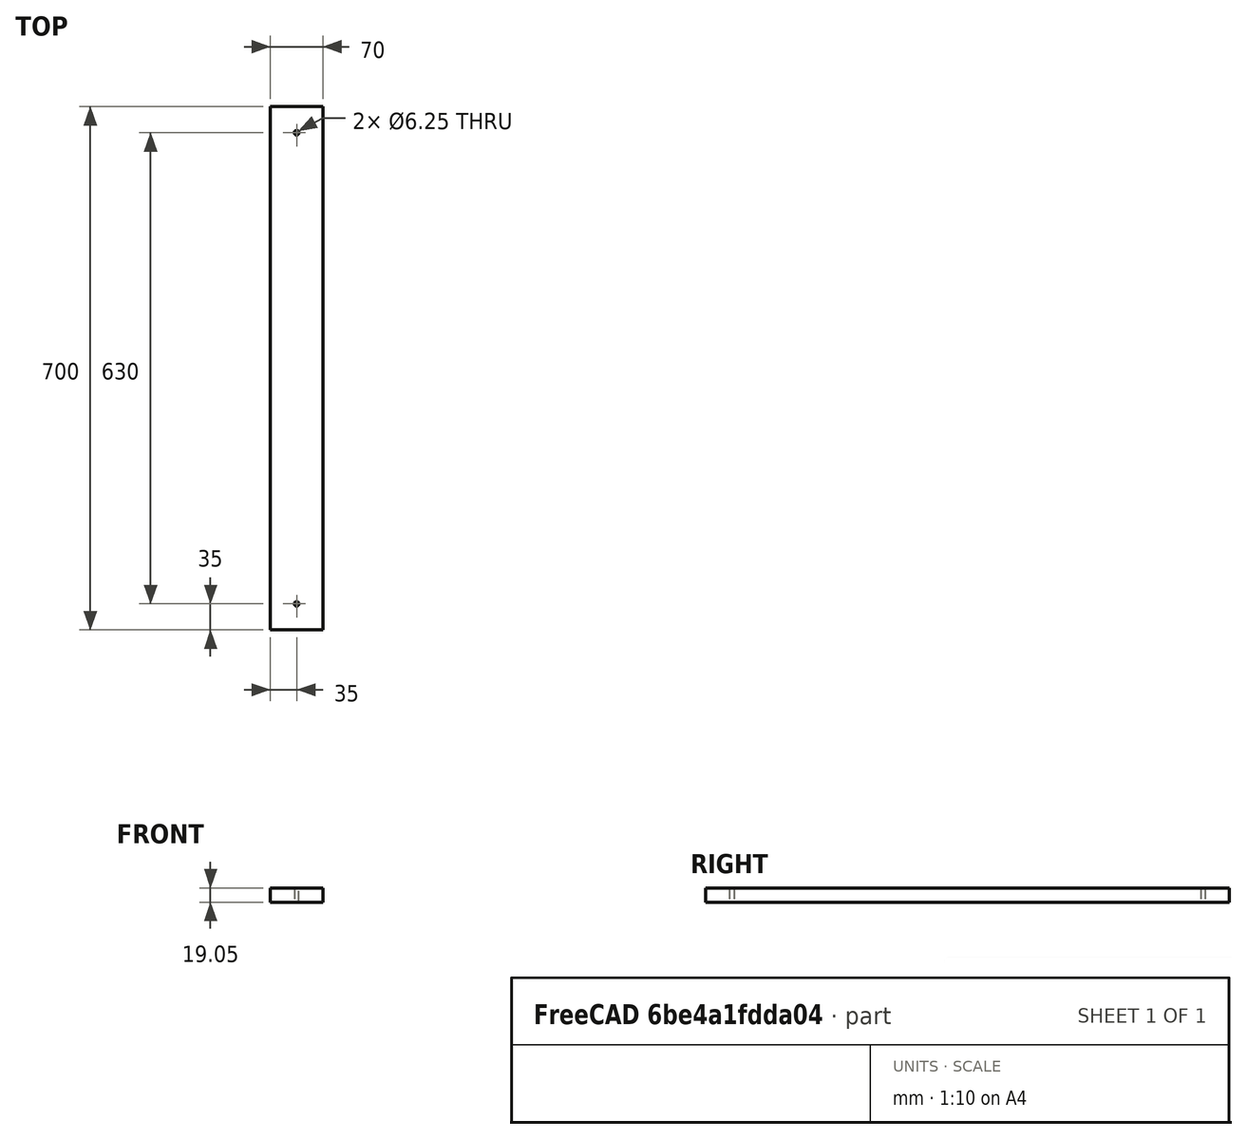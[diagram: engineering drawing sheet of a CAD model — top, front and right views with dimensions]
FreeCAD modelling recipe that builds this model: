
FCSTD DOCUMENT  (FreeCAD 0.20R29410 (Git))
Label: foot
License: All rights reserved
LicenseURL: http://en.wikipedia.org/wiki/All_rights_reserved
objects: Sketcher::SketchObject×1, PartDesign::Pad×1, PartDesign::Body×1
note: 4 computed .brp shape members not serialized (recipe doc carries the construction recipe); baked Part::Feature solids carry a one-line shape summary decoded from their .brp

FEATURE [Sketcher::SketchObject] Sketch
  FullyConstrained = true
  MapMode = 5
  Support = -> [XY_Plane]
  sketch-geometry (14):
    g0: LineSegment StartX=-35 StartY=350 StartZ=0 EndX=35 EndY=350 EndZ=0
    g1: LineSegment StartX=35 StartY=350 StartZ=0 EndX=35 EndY=-350 EndZ=0
    g2: LineSegment StartX=35 StartY=-350 StartZ=0 EndX=-35 EndY=-350 EndZ=0
    g3: LineSegment StartX=-35 StartY=-350 StartZ=0 EndX=-35 EndY=350 EndZ=0
    g4: Circle CenterX=6e-16 CenterY=315 CenterZ=0 NormalX=0 NormalY=0 NormalZ=1 AngleXU=0 Radius=3.125
    g5: Circle CenterX=0 CenterY=-315 CenterZ=0 NormalX=0 NormalY=0 NormalZ=1 AngleXU=0 Radius=3.125
    g6: LineSegment StartX=-35 StartY=-280 StartZ=0 EndX=35 EndY=-280 EndZ=0
    g7: LineSegment StartX=35 StartY=-280 StartZ=0 EndX=35 EndY=-350 EndZ=0
    g8: LineSegment StartX=35 StartY=-350 StartZ=0 EndX=-35 EndY=-350 EndZ=0
    g9: LineSegment StartX=-35 StartY=-350 StartZ=0 EndX=-35 EndY=-280 EndZ=0
    g10: LineSegment StartX=-35 StartY=350 StartZ=0 EndX=35 EndY=350 EndZ=0
    g11: LineSegment StartX=35 StartY=350 StartZ=0 EndX=35 EndY=280 EndZ=0
    g12: LineSegment StartX=35 StartY=280 StartZ=0 EndX=-35 EndY=280 EndZ=0
    g13: LineSegment StartX=-35 StartY=280 StartZ=0 EndX=-35 EndY=350 EndZ=0
  constraints (40):
    c: Coincident(g0,g1)
    c: Coincident(g1,g2)
    c: Coincident(g2,g3)
    c: Coincident(g3,g0)
    c: Horizontal(g0)
    c: Horizontal(g2)
    c: Vertical(g1)
    c: Vertical(g3)
    c: DistanceY(g-1,g4) = 315
    c: DistanceY(g5,g-1) = 315
    c: Coincident(g6,g7)
    c: Coincident(g7,g8)
    c: Coincident(g8,g9)
    c: Coincident(g9,g6)
    c: Horizontal(g6)
    c: Horizontal(g8)
    c: Vertical(g7)
    c: Vertical(g9)
    c: Symmetric(g6,g7,g5)
    c: PointOnObject(g5,g-2)
    c: PointOnObject(g4,g-2)
    c: DistanceX(g8,g8) = 70
    c: Equal(g8,g9)
    c: Coincident(g10,g11)
    c: Coincident(g11,g12)
    c: Coincident(g12,g13)
    c: Coincident(g13,g10)
    c: Horizontal(g10)
    c: Horizontal(g12)
    c: Vertical(g11)
    c: Vertical(g13)
    c: DistanceX(g10,g10) = 70
    c: Equal(g10,g11)
    c: Symmetric(g12,g10,g4)
    c: Coincident(g2,g8)
    c: Coincident(g0,g10)
    c: Diameter(g4) = 6.25
    c: Diameter(g5) = 6.25
    c: DistanceY(g1,g0) = 700
    c: DistanceY(g4,g0) = 35
FEATURE [PartDesign::Pad] Pad
  Direction = (0,0,1)
  Length = 19.05
  Length2 = 10
  Profile = -> Sketch
  ReferenceAxis = -> Sketch [N_Axis]
  Type = 0
  expr: Length = 3 / 4 * 25.4
FEATURE [PartDesign::Body] Body
  Group = -> [Sketch,Pad]
  Origin = -> Origin
  Tip = -> Pad
